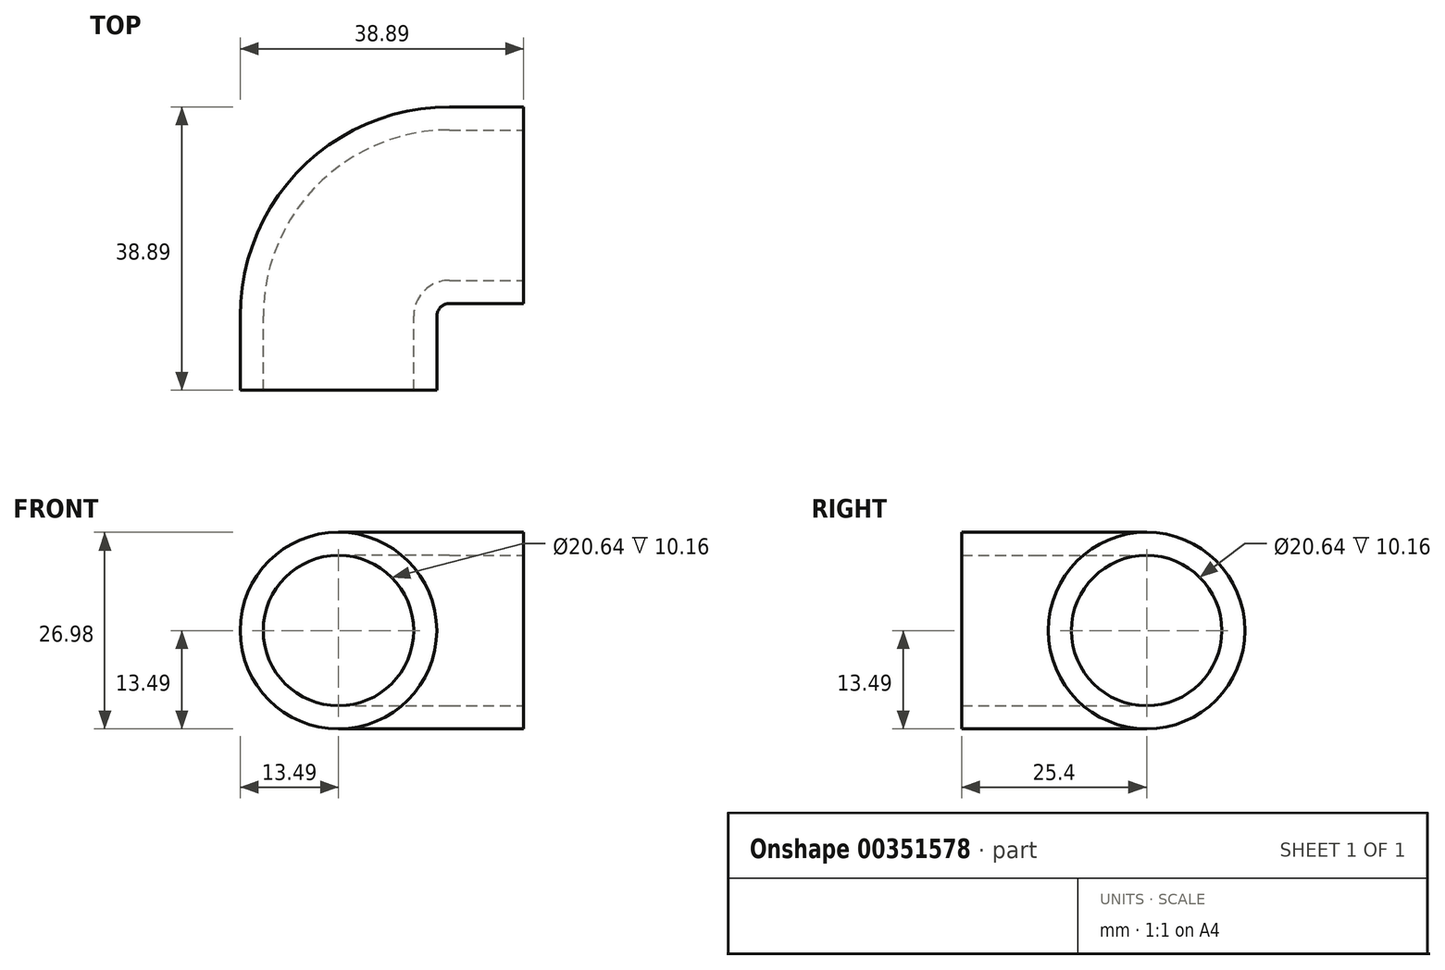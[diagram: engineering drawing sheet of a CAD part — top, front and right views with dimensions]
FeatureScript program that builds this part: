
annotation { "Feature Type Name" : "Feature", "Feature Type Description" : "" }
export const myFeature = defineFeature(function(context is Context, id is Id, definition is map)
    precondition{}
    {
        {
            var Q0;
            Q0=qCreatedBy(makeId("Top.planeOp"),FACE);
            var sketch = newSketch(context, id + "F0", { "sketchPlane" : qUnion([Q0])});
            skLineSegment(sketch, "E0", {"start": v(0, 0) * mm, "end": v(0, 10.16) * mm});
            skLineSegment(sketch, "E1", {"start": v(15.24, 25.4) * mm, "end": v(25.4, 25.4) * mm});
            skArc(sketch, "E2.filletArc", {"start": v(15.24, 25.4) * mm, "mid": v(4.46, 20.94) * mm, "end": v(0, 10.16) * mm});
            skLineSegment(sketch, "E3", {"start": v(0, 0) * mm, "end": v(-13.5, 0) * mm, "construction": true});
            skLineSegment(sketch, "E4", {"start": v(-13.5, 0) * mm, "end": v(-13.5, 62.53) * mm, "construction": true});
            skSolve(sketch);
        }
        {
            var Q0;
            Q0=qCreatedBy(makeId("Front.planeOp"),FACE);
            var sketch = newSketch(context, id + "F1", { "sketchPlane" : qUnion([Q0])});
            skCircle(sketch, "E5", {"center": v(0, 0) * mm, "radius": 13.5 * mm});
            skSolve(sketch);
        }
        {
            var Q0;
            Q0 = qSketchRegion(id + "F1", true);
            var Q1;
            Q1 = qConstructionFilter(qBodyType(qCreatedBy(id + "F0" ,EDGE), BodyType.WIRE), ConstructionObject.NO);
            sweep(context, id + "F2", {"profiles" : qUnion([Q0]), "path" : qUnion([Q1])});
        }
        {
            var Q0;
            Q0=makeQuery(id+"F2.opSweep","CAP_FACE",FACE,{"disambiguationData":[OSD([sQuery(id+"F0.wireOp",VERTEX,"E0.start"),sQuery(id+"F1.wireOp",EDGE,"E5")])],"isStart":true});
            var Q1;
            Q1=makeQuery(id+"F2.opSweep","CAP_FACE",FACE,{"disambiguationData":[OSD([sQuery(id+"F0.wireOp",VERTEX,"E1.end"),sQuery(id+"F1.wireOp",EDGE,"E5")])],"isStart":false});
            var Q2;
            Q2=makeQuery(id+"F2.opSweep","SWEPT_BODY",BODY,{"disambiguationData":[OSD([sQuery(id+"F0.wireOp",EDGE,"E0"),sQuery(id+"F1.wireOp",EDGE,"E5")])]});
            shell(context, id + "F3", {"entities" : qUnion([Q0, Q1]), "parts" : qUnion([Q2]), "thickness" : 3.17 * mm});
        }
    });
